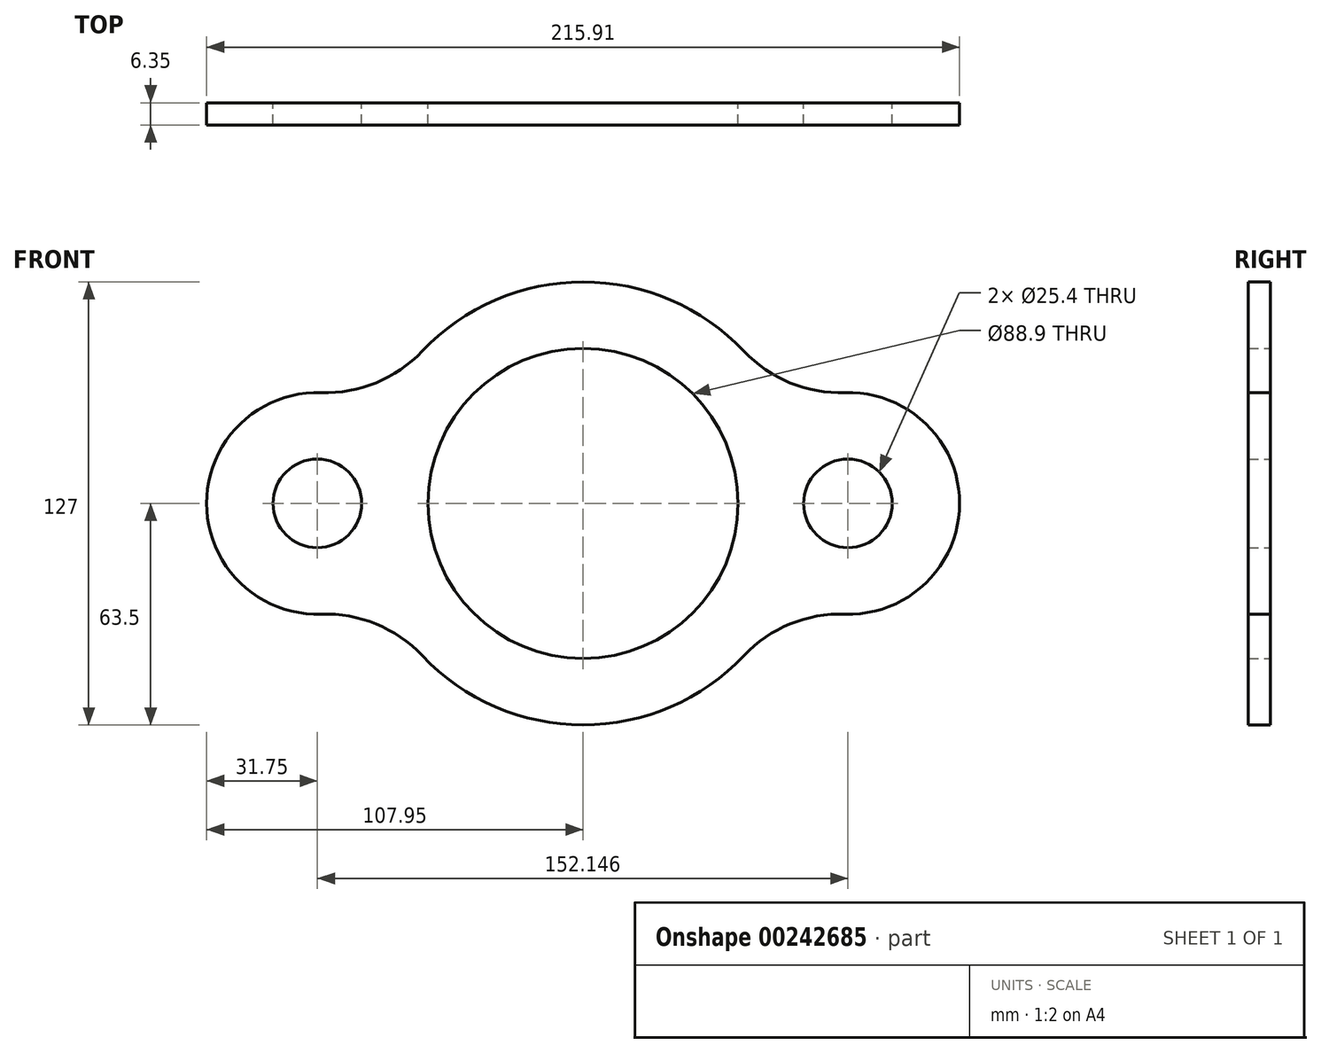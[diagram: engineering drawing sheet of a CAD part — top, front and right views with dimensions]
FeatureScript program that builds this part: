
annotation { "Feature Type Name" : "Feature", "Feature Type Description" : "" }
export const myFeature = defineFeature(function(context is Context, id is Id, definition is map)
    precondition{}
    {
        {
            var Q0;
            Q0=qCreatedBy(makeId("Front.planeOp"),FACE);
            var sketch = newSketch(context, id + "F0", { "sketchPlane" : qUnion([Q0])});
            skArc(sketch, "E0", {"start": v(-46.14, -43.63) * mm, "mid": v(0, -63.5) * mm, "end": v(46.13, -43.64) * mm});
            skPoint(sketch, "E1", {"position": v(75.95, 0) * mm});
            skPoint(sketch, "E2", {"position": v(-76.2, 0) * mm});
            skCircle(sketch, "E3", {"center": v(75.95, 0) * mm, "radius": 12.7 * mm});
            skCircle(sketch, "E4", {"center": v(-76.2, 0) * mm, "radius": 12.7 * mm});
            skArc(sketch, "E5", {"start": v(-75.12, 31.73) * mm, "mid": v(-107.95, 0) * mm, "end": v(-75.12, -31.73) * mm});
            skPoint(sketch, "E6.visualSharp", {"position": v(-57.94, 25.98) * mm});
            skArc(sketch, "E6.filletArc", {"start": v(-75.12, 31.73) * mm, "mid": v(-59.35, 34.56) * mm, "end": v(-46.14, 43.63) * mm});
            skPoint(sketch, "E7.visualSharp", {"position": v(-57.94, -25.98) * mm});
            skArc(sketch, "E7.filletArc", {"start": v(-46.14, -43.63) * mm, "mid": v(-59.35, -34.56) * mm, "end": v(-75.12, -31.73) * mm});
            skArc(sketch, "E8.trimOffspring", {"start": v(75.11, -31.74) * mm, "mid": v(107.96, 0) * mm, "end": v(75.11, 31.74) * mm});
            skArc(sketch, "E9.trimOffspring", {"start": v(46.13, 43.64) * mm, "mid": v(0, 63.5) * mm, "end": v(-46.14, 43.63) * mm});
            skPoint(sketch, "E10.visualSharp", {"position": v(57.94, 25.98) * mm});
            skArc(sketch, "E10.filletArc", {"start": v(46.13, 43.64) * mm, "mid": v(59.34, 34.57) * mm, "end": v(75.11, 31.74) * mm});
            skPoint(sketch, "E11.visualSharp", {"position": v(57.94, -25.98) * mm});
            skArc(sketch, "E11.filletArc", {"start": v(75.11, -31.74) * mm, "mid": v(59.34, -34.57) * mm, "end": v(46.13, -43.64) * mm});
            skCircle(sketch, "E12", {"center": v(0, 0) * mm, "radius": 44.45 * mm});
            skSolve(sketch);
        }
        {
            var Q0;
            Q0 = qSketchRegion(id + "F0", true);
            extrude(context, id + "F1", {"entities" : qUnion([Q0]), "depth" : 6.35 * mm});
        }
    });
